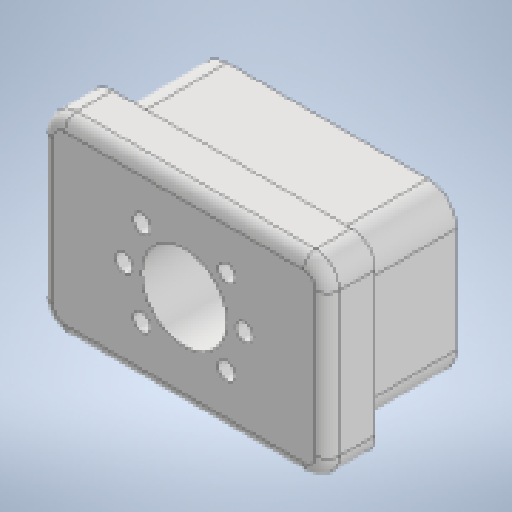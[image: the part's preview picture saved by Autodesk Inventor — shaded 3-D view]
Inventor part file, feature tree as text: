
AUTODESK INVENTOR PART (.ipt)
format: ipt  version: 2023 (Build 270158000, 158)  size: 201,728 bytes
history: native  units: in
note: dims shown in document units (in); Inventor stores cm internally (conversion verified against a paired STEP export)
features: extrude x3, sketch x3, fillet x1
ambient origin geometry x8: Origin, YZ Plane, XZ Plane, XY Plane, X Axis, Y Axis, Z Axis, Center Point
bodies: Solid1 (feature_tree)
feature tree (7):
  extrude  "Extrusion1"  Depth=1.7in
  extrude  "Extrusion2"  Depth=1.0in TaperAngle=0.0deg
  fillet  "Fillet1"  Radius=3.0in
  extrude  "Extrusion3"  Depth=0.25in
  sketch  "Sketch1"  dims[d0=2.7in d1=1.7in]
  sketch  "Sketch2"  dims[d3=0.3in d4=1.0in d5=0.0in d6=3.0in]
  sketch  "Sketch3"  dims[d7=2.0in d8=0.25in d9=0.5in d10=0.0in d11=0.125in d12=0.8858in d13=1.2598in d14=0.1811in d15=45.0deg d16=0.5in d17=0.0in]
